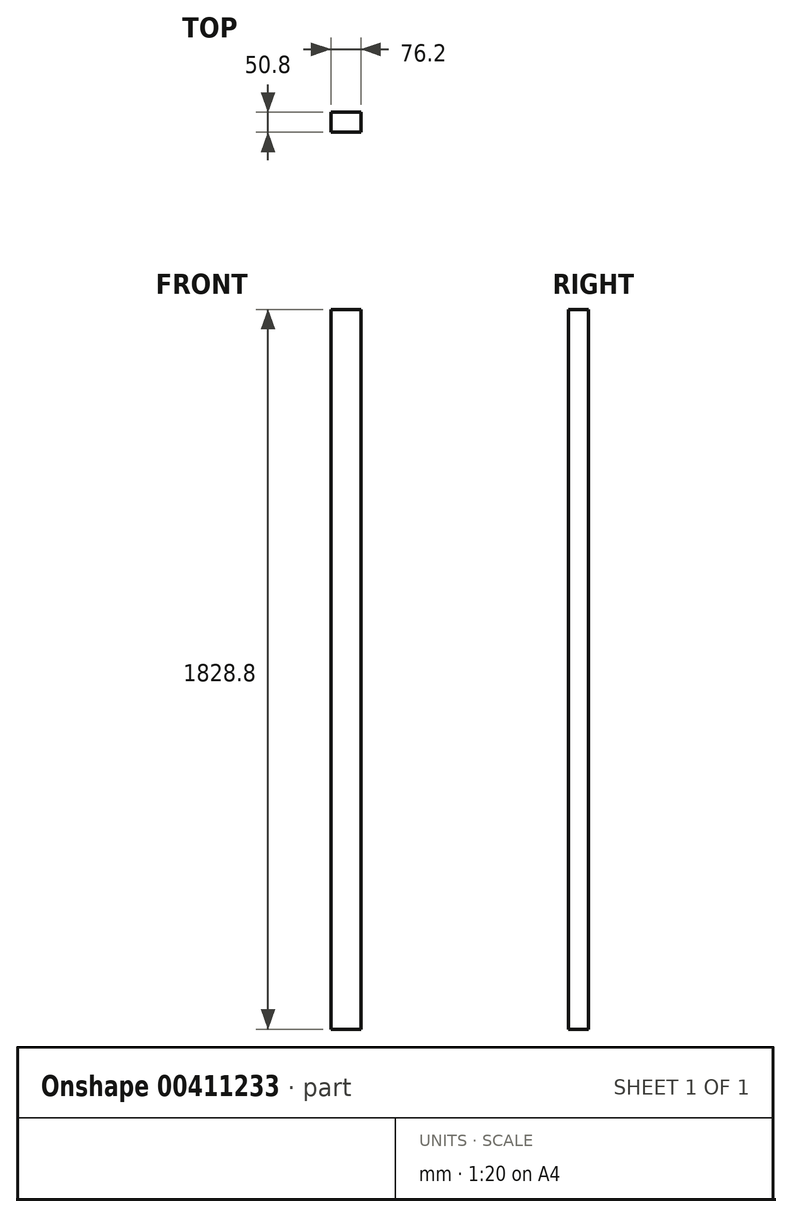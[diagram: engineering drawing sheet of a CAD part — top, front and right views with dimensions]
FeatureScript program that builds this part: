
annotation { "Feature Type Name" : "Feature", "Feature Type Description" : "" }
export const myFeature = defineFeature(function(context is Context, id is Id, definition is map)
    precondition{}
    {
        {
            var Q0;
            Q0=qCreatedBy(makeId("Top.planeOp"),FACE);
            var sketch = newSketch(context, id + "F0", { "sketchPlane" : qUnion([Q0])});
            skLineSegment(sketch, "E0.bottom", {"start": v(38.1, -25.4) * mm, "end": v(-38.1, -25.4) * mm});
            skLineSegment(sketch, "E0.top", {"start": v(38.1, 25.4) * mm, "end": v(-38.1, 25.4) * mm});
            skLineSegment(sketch, "E0.left", {"start": v(38.1, -25.4) * mm, "end": v(38.1, 25.4) * mm});
            skLineSegment(sketch, "E0.right", {"start": v(-38.1, -25.4) * mm, "end": v(-38.1, 25.4) * mm});
            skPoint(sketch, "E0.middle", {"position": v(0, 0) * mm});
            skSolve(sketch);
        }
        {
            var Q0;
            Q0 = qSketchRegion(id + "F0", true);
            extrude(context, id + "F1", {"entities" : qUnion([Q0]), "depth" : 1828.8 * mm});
        }
    });
